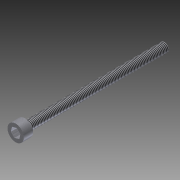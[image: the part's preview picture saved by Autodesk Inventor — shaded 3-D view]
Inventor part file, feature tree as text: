
AUTODESK INVENTOR PART (.ipt)
format: ipt  version: 2012 (Build 160160000, 160)  size: 96,256 bytes
history: native  units: in
note: dims shown in document units (in); Inventor stores cm internally (conversion verified against a paired STEP export)
features: extrude x2, sketch x1, thread x1
ambient origin geometry x8: Origin, YZ Plane, XZ Plane, XY Plane, X Axis, Y Axis, Z Axis, Center Point
bodies: Solid1 (feature_tree)
feature tree (4):
  sketch  "Sketch1"  dims[d0=0.19in d1=0.35in d2=3.0in d3=0.0in d4=0.2in d5=0.0in d6=1.0in d7=0.0in]
  extrude  "Extrusion1"  Depth=0.35in
  extrude  "Extrusion2"  Depth=3.0in TaperAngle=0.0deg
  thread  "Thread1"  [1 undecoded]
note: 1 required parameter value undecoded (feature->parameter linkage not recoverable at this tier; creation-order binding heuristic only, values carry confidence <= 0.55)
